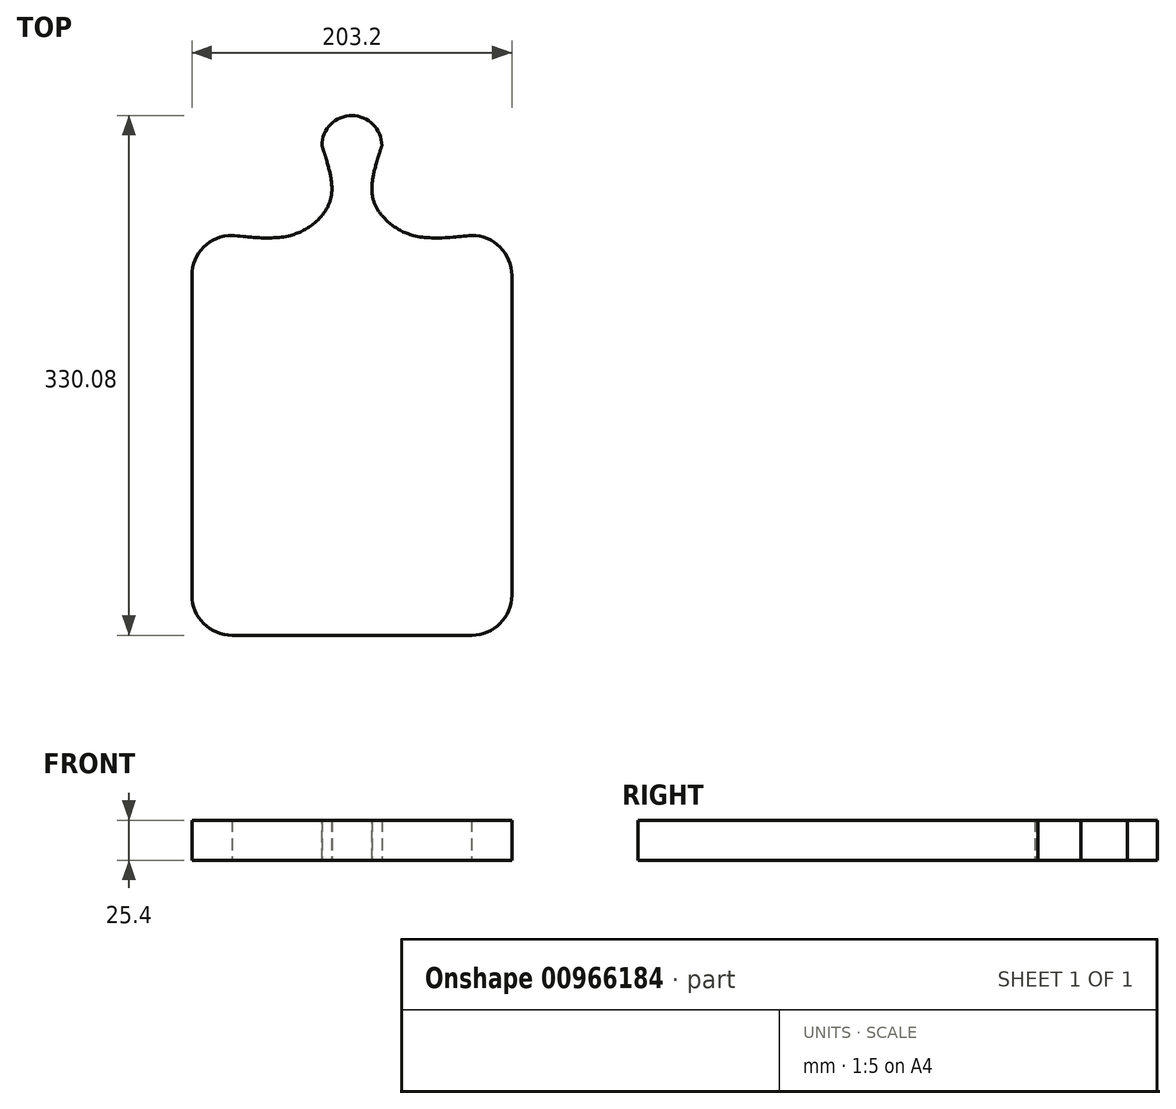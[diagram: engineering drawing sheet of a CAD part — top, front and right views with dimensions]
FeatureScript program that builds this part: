
annotation { "Feature Type Name" : "Feature", "Feature Type Description" : "" }
export const myFeature = defineFeature(function(context is Context, id is Id, definition is map)
    precondition{}
    {
        {
            var Q0;
            Q0=qCreatedBy(makeId("Top.planeOp"),FACE);
            var sketch = newSketch(context, id + "F0", { "sketchPlane" : qUnion([Q0])});
            skPoint(sketch, "E0", {"position": v(0, 76.2) * mm});
            skPoint(sketch, "E1", {"position": v(-19.05, 76.2) * mm});
            skPoint(sketch, "E2", {"position": v(-19.05, 0) * mm});
            skPoint(sketch, "E3", {"position": v(-101.6, 0) * mm});
            skPoint(sketch, "E4", {"position": v(-101.6, -254) * mm});
            skPoint(sketch, "E5", {"position": v(0, -254) * mm});
            skLineSegment(sketch, "E6", {"start": v(-41.9, 0) * mm, "end": v(-38.96, 0) * mm});
            skLineSegment(sketch, "E7", {"start": v(-101.6, -25.58) * mm, "end": v(-101.6, -228.53) * mm});
            skLineSegment(sketch, "E8", {"start": v(-76.17, -254) * mm, "end": v(0, -254) * mm});
            skLineSegment(sketch, "E9.MirrorCS", {"start": v(101.6, -25.58) * mm, "end": v(101.6, -228.53) * mm});
            skLineSegment(sketch, "E10.MirrorCS", {"start": v(76.17, -254) * mm, "end": v(0, -254) * mm});
            skPoint(sketch, "E11.1.internal.snap0", {"position": v(-19.05, 6.31) * mm});
            skLineSegment(sketch, "E12", {"start": v(0, 76.2) * mm, "end": v(0, 51) * mm});
            skLineSegment(sketch, "E13", {"start": v(0, 76.2) * mm, "end": v(0, 57.03) * mm});
            skArc(sketch, "E14", {"start": v(15.62, 46.12) * mm, "mid": v(0, 76.08) * mm, "end": v(-15.62, 46.12) * mm});
            skArc(sketch, "E15.MirrorC", {"start": v(-15.62, 46.12) * mm, "mid": v(0, 76.08) * mm, "end": v(15.62, 46.12) * mm});
            skFitSpline(sketch, "E16.MirrorCS", {"points": [v(19.05, 57.03) * mm, v(12.8, 27.54) * mm, v(19.05, 12.63) * mm], "startDerivative": vector(-18.2, -55.65) * mm, "endDerivative": vector(20.18, -31.93) * mm});
            skFitSpline(sketch, "E17.MirrorCS", {"points": [v(12.8, 27.54) * mm, v(19.05, 12.63) * mm, v(38.96, 0) * mm], "startDerivative": vector(8.67, -35.15) * mm, "endDerivative": vector(42.58, -20.4) * mm});
            skPoint(sketch, "E18.MirrorCS.start.orphan", {"position": v(30.48, 0) * mm});
            skArc(sketch, "E19", {"start": v(-76.1, 0) * mm, "mid": v(-94.14, -7.52) * mm, "end": v(-101.6, -25.58) * mm});
            skArc(sketch, "E20.MirrorCS", {"start": v(76.1, 0) * mm, "mid": v(94.14, -7.52) * mm, "end": v(101.6, -25.58) * mm});
            skArc(sketch, "E21", {"start": v(-101.6, -228.53) * mm, "mid": v(-94.13, -246.55) * mm, "end": v(-76.1, -254) * mm});
            skPoint(sketch, "E22.orphan", {"position": v(101.6, 0) * mm});
            skArc(sketch, "E23.MirrorCS", {"start": v(101.6, -228.53) * mm, "mid": v(94.13, -246.55) * mm, "end": v(76.1, -254) * mm});
            skPoint(sketch, "E24.orphan", {"position": v(101.6, -254) * mm});
            skPoint(sketch, "E25.orphan", {"position": v(-19.05, 38.1) * mm});
            skFitSpline(sketch, "E26", {"points": [v(19.05, 57.03) * mm, v(15.62, 46.12) * mm, v(12.8, 27.54) * mm, v(19.05, 12.63) * mm, v(38.96, 0) * mm, v(76.1, 0) * mm], "startDerivative": vector(-22.47, -66.8) * mm, "endDerivative": vector(147.8, 15.82) * mm});
            skPoint(sketch, "E27.end.orphan", {"position": v(-38.96, 0) * mm});
            skPoint(sketch, "E28.2.internal.orphan", {"position": v(-19.05, 12.63) * mm});
            skFitSpline(sketch, "E29.MirrorCS", {"points": [v(-19.05, 57.03) * mm, v(-12.8, 27.54) * mm, v(-19.05, 12.63) * mm], "startDerivative": vector(18.2, -55.65) * mm, "endDerivative": vector(-20.18, -31.93) * mm});
            skFitSpline(sketch, "E30.MirrorCS", {"points": [v(-12.8, 27.54) * mm, v(-19.05, 12.63) * mm, v(-38.96, 0) * mm], "startDerivative": vector(-8.67, -35.15) * mm, "endDerivative": vector(-42.58, -20.4) * mm});
            skFitSpline(sketch, "E31.MirrorCS", {"points": [v(-19.05, 57.03) * mm, v(-15.62, 46.12) * mm, v(-12.8, 27.54) * mm, v(-19.05, 12.63) * mm, v(-38.96, 0) * mm, v(-76.1, 0) * mm], "startDerivative": vector(22.47, -66.8) * mm, "endDerivative": vector(-147.8, 15.82) * mm});
            skPoint(sketch, "E32.orphan", {"position": v(19.05, 0) * mm});
            skPoint(sketch, "E33.end.orphan", {"position": v(-30.48, 0) * mm});
            skSolve(sketch);
        }
        {
            var Q0;
            {var subQ7=sQuery(id+"F0.wireOp",EDGE,"E7");Q0=makeQuery(id+"F0.imprint","IMPRINT",FACE,{"disambiguationData":[TD([[makeQuery(id+"F0.imprint","IMPRINT",EDGE,{"derivedFrom":subQ7}),1.0]])]});}
            extrude(context, id + "F1", {"entities" : qUnion([Q0]), "depth" : 25.4 * mm, "offsetDistance" : 25.4 * mm});
        }
    });
